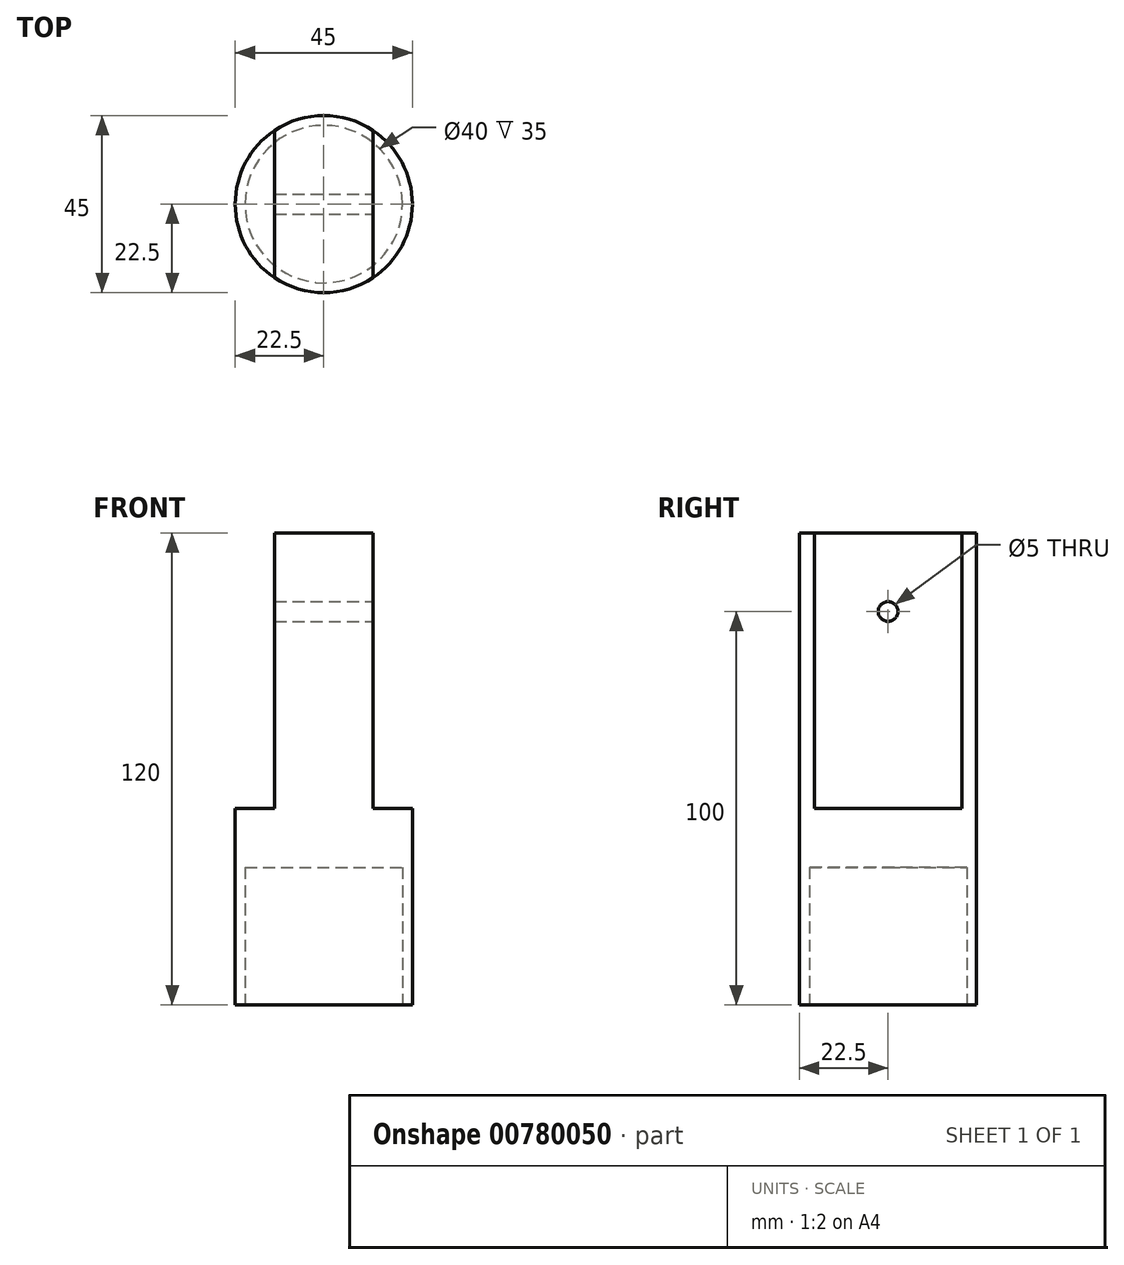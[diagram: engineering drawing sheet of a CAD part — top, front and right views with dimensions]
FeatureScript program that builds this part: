
annotation { "Feature Type Name" : "Feature", "Feature Type Description" : "" }
export const myFeature = defineFeature(function(context is Context, id is Id, definition is map)
    precondition{}
    {
        {
            var Q0;
            Q0=qCreatedBy(makeId("Top.planeOp"),FACE);
            var sketch = newSketch(context, id + "F0", { "sketchPlane" : qUnion([Q0])});
            skCircle(sketch, "E0", {"center": v(0, 0) * mm, "radius": 22.5 * mm});
            skSolve(sketch);
        }
        {
            var Q0;
            Q0=makeQuery(id+"F0.imprint","IMPRINT",FACE,{"disambiguationData":[TD([[makeQuery(id+"F0.imprint","IMPRINT",EDGE,{"derivedFrom":sQuery(id+"F0.wireOp",EDGE,"E0")}),1.0]])]});
            extrude(context, id + "F1", {"entities" : qUnion([Q0]), "depth" : 120 * mm, "offsetDistance" : 25 * mm});
        }
        {
            var Q0;
            Q0=makeQuery(id+"F1.opExtrude","CAP_FACE",FACE,{"disambiguationData":[OSD([sQuery(id+"F0.wireOp",EDGE,"E0")])],"isStart":false});
            var sketch = newSketch(context, id + "F2", { "sketchPlane" : qUnion([Q0])});
            skLineSegment(sketch, "E1", {"start": v(-12.5, 18.7) * mm, "end": v(-12.5, -18.7) * mm});
            skLineSegment(sketch, "E2", {"start": v(12.5, 18.7) * mm, "end": v(12.5, -18.7) * mm});
            skSolve(sketch);
        }
        {
            var Q0;
            Q0=makeQuery(id+"F1.opExtrude","CAP_FACE",FACE,{"disambiguationData":[OSD([sQuery(id+"F0.wireOp",EDGE,"E0")])],"isStart":false});
            var sketch = newSketch(context, id + "F3", { "sketchPlane" : qUnion([Q0])});
            skLineSegment(sketch, "E3", {"start": v(-12.5, 18.7) * mm, "end": v(-12.5, -18.7) * mm});
            skLineSegment(sketch, "E4", {"start": v(12.5, 18.7) * mm, "end": v(12.5, -18.7) * mm});
            skSolve(sketch);
        }
        {
            var Q0;
            {var subQ0=sQuery(id+"F2.wireOp",EDGE,"E1");Q0=makeQuery(id+"F2.imprint","IMPRINT",FACE,{"disambiguationData":[TD([[makeQuery(id+"F2.imprint","IMPRINT",EDGE,{"derivedFrom":subQ0}),-1.0]])]});}
            var Q1;
            {var subQ0=sQuery(id+"F2.wireOp",EDGE,"E2");Q1=makeQuery(id+"F2.imprint","IMPRINT",FACE,{"disambiguationData":[TD([[makeQuery(id+"F2.imprint","IMPRINT",EDGE,{"derivedFrom":subQ0}),1.0]])]});}
            extrude(context, id + "F4", {"entities" : qUnion([Q0, Q1]), "operationType" : NewBodyOperationType.REMOVE, "oppositeDirection" : true, "depth" : 70 * mm, "offsetDistance" : 25 * mm});
        }
        {
            var Q0;
            Q0=makeQuery(id+"F1.opExtrude","CAP_FACE",FACE,{"disambiguationData":[OSD([sQuery(id+"F0.wireOp",EDGE,"E0")])],"isStart":true});
            var sketch = newSketch(context, id + "F5", { "sketchPlane" : qUnion([Q0])});
            skCircle(sketch, "E5", {"center": v(0, 0) * mm, "radius": 20 * mm});
            skSolve(sketch);
        }
        {
            var Q0;
            Q0=makeQuery(id+"F5.imprint","IMPRINT",FACE,{"disambiguationData":[TD([[makeQuery(id+"F5.imprint","IMPRINT",EDGE,{"derivedFrom":sQuery(id+"F5.wireOp",EDGE,"E5")}),1.0]])]});
            extrude(context, id + "F6", {"entities" : qUnion([Q0]), "operationType" : NewBodyOperationType.REMOVE, "oppositeDirection" : true, "depth" : 35 * mm, "offsetDistance" : 25 * mm});
        }
        {
            var Q0;
            Q0=qCreatedBy(makeId("Right.planeOp"),FACE);
            cPlane(context, id + "F7", {"entities" : qUnion([Q0]), "cplaneType" : CPlaneType.OFFSET, "offset" : 22.5 * mm, "width" : 150 * mm, "height" : 150 * mm});
        }
        {
            var Q0;
            Q0=qCreatedBy(id+"F7.planeOp",FACE);
            var sketch = newSketch(context, id + "F8", { "sketchPlane" : qUnion([Q0])});
            skLineSegment(sketch, "E6", {"start": v(-18.7, 100) * mm, "end": v(18.7, 100) * mm});
            skPoint(sketch, "E7", {"position": v(0, 100) * mm});
            skSolve(sketch);
        }
        {
            var Q0;
            Q0=sQuery(id+"F8.wireOp",VERTEX,"E7");
            var Q1;
            Q1=makeQuery(id+"F1.opExtrude","SWEPT_BODY",BODY,{"disambiguationData":[OSD([sQuery(id+"F0.wireOp",EDGE,"E0")])]});
            hole(context, id + "F9", {"style" : HoleStyle.SIMPLE, "endStyle" : HoleEndStyle.THROUGH, "holeDiameter" : 5 * mm, "majorDiameter" : 5 * mm, "isTappedThrough" : true, "tappedDepth" : 12 * mm, "tapClearance" : 3, "locations" : qUnion([Q0]), "scope" : qUnion([Q1])});
        }
    });
